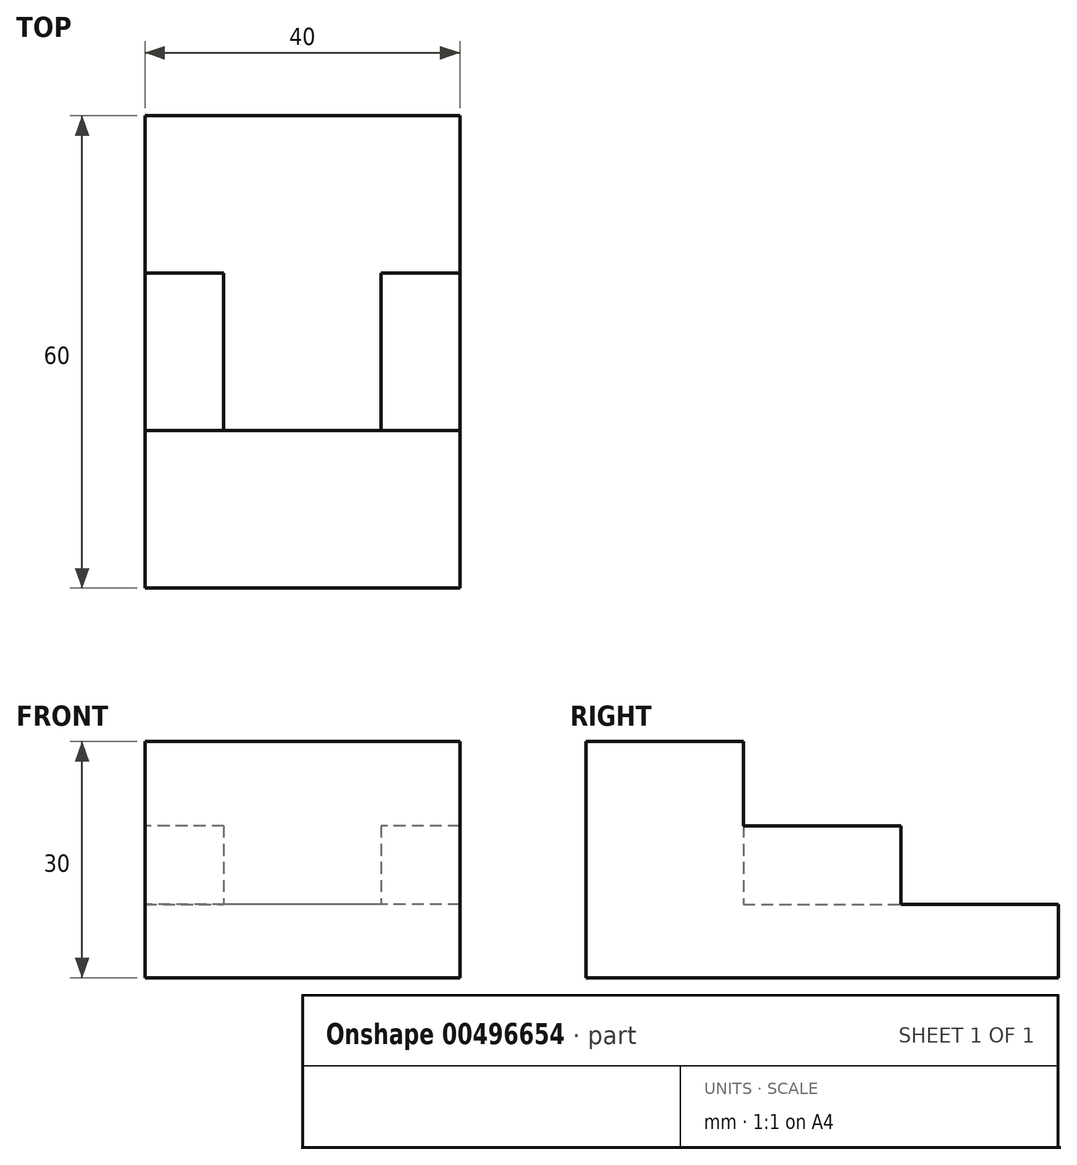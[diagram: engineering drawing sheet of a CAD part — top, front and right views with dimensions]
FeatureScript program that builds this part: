
annotation { "Feature Type Name" : "Feature", "Feature Type Description" : "" }
export const myFeature = defineFeature(function(context is Context, id is Id, definition is map)
    precondition{}
    {
        {
            var Q0;
            Q0=qCreatedBy(makeId("Right.planeOp"),FACE);
            var sketch = newSketch(context, id + "F0", { "sketchPlane" : qUnion([Q0])});
            skLineSegment(sketch, "E0", {"start": v(0, 0) * mm, "end": v(0, 30) * mm});
            skLineSegment(sketch, "E1", {"start": v(0, 0) * mm, "end": v(60, 0) * mm});
            skLineSegment(sketch, "E2", {"start": v(60, -0.7) * mm, "end": v(60, 9.3) * mm});
            skLineSegment(sketch, "E3", {"start": v(60, 9.3) * mm, "end": v(50, 9.3) * mm});
            skLineSegment(sketch, "E4", {"start": v(0, 30) * mm, "end": v(20, 30) * mm});
            skLineSegment(sketch, "E5", {"start": v(20, 30) * mm, "end": v(20, 9.3) * mm});
            skLineSegment(sketch, "E6", {"start": v(20, 9.3) * mm, "end": v(50, 9.3) * mm});
            skSolve(sketch);
        }
        {
            var Q0;
            Q0 = qSketchRegion(id + "F0", true);
            extrude(context, id + "F1", {"entities" : qUnion([Q0]), "depth" : 40 * mm});
        }
        {
            var Q0;
            Q0=makeQuery(id+"F1.opExtrude","SWEPT_FACE",FACE,{"disambiguationData":[OSD([sQuery(id+"F0.wireOp",EDGE,"E3"),sQuery(id+"F0.wireOp",EDGE,"E6")])]});
            var sketch = newSketch(context, id + "F2", { "sketchPlane" : qUnion([Q0])});
            skLineSegment(sketch, "E7.bottom", {"start": v(40, 20) * mm, "end": v(30, 20) * mm});
            skLineSegment(sketch, "E7.top", {"start": v(40, 40) * mm, "end": v(30, 40) * mm});
            skLineSegment(sketch, "E7.left", {"start": v(40, 20) * mm, "end": v(40, 40) * mm});
            skLineSegment(sketch, "E7.right", {"start": v(30, 20) * mm, "end": v(30, 40) * mm});
            skLineSegment(sketch, "E8.bottom", {"start": v(0, 20) * mm, "end": v(10, 20) * mm});
            skLineSegment(sketch, "E8.top", {"start": v(0, 40) * mm, "end": v(10, 40) * mm});
            skLineSegment(sketch, "E8.left", {"start": v(0, 20) * mm, "end": v(0, 40) * mm});
            skLineSegment(sketch, "E8.right", {"start": v(10, 20) * mm, "end": v(10, 40) * mm});
            skSolve(sketch);
        }
        {
            var Q0;
            Q0 = qSketchRegion(id + "F2", true);
            extrude(context, id + "F3", {"entities" : qUnion([Q0]), "operationType" : NewBodyOperationType.ADD, "depth" : 10 * mm});
        }
    });
